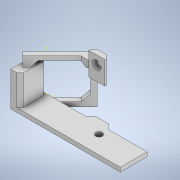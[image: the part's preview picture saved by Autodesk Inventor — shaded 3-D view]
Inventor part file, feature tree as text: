
AUTODESK INVENTOR PART (.ipt)
format: ipt  version: 2021.2 (Build 252289000, 289)  size: 273,408 bytes
history: native  units: in
note: dims shown in document units (in); Inventor stores cm internally (conversion verified against a paired STEP export)
features: sketch x20, extrude x15, chamfer x4
ambient origin geometry x8: Origin, YZ Plane, XZ Plane, XY Plane, X Axis, Y Axis, Z Axis, Center Point
bodies: Solid1 (feature_tree)
feature tree (39):
  extrude  "Extrusion1"  Depth=0.16in
  extrude  "Extrusion2"  Depth=1.0in
  chamfer  "Chamfer1"  Distance=0.1875in
  extrude  "Extrusion3"  Depth=0.125in TaperAngle=0.0deg
  extrude  "Extrusion4"  Depth=0.125in TaperAngle=0.0deg
  sketch  "Sketch5"  dims[d9=0.125in d10=0.125in d11=45.0deg d12=0.5625in d13=0.0in]
  chamfer  "Chamfer2"  Distance=0.125in Angle=45.0deg
  sketch  "Sketch6"  dims[d14=0.33in d15=0.5625in d16=0.0in d17=0.125in d18=0.125in d19=45.0deg]
  extrude  "Extrusion5"  Depth=0.816in
  sketch  "Sketch8"  dims[d23=0.1in d24=0.0in d26=0.2875in d27=0.0in]
  extrude  "Extrusion6"  Depth=0.1in TaperAngle=0.0deg
  extrude  "Extrusion7"  Depth=1.7875in TaperAngle=0.0deg
  sketch  "Sketch11"  dims[d36=21112.9in d37=0.0in d38=1.5in d39=0.0in]
  extrude  "Extrusion8"  Depth=0.35in TaperAngle=0.0deg
  extrude  "Extrusion9"  Depth=1.5in TaperAngle=0.0deg
  extrude  "Extrusion10"  Depth=1.01in TaperAngle=0.0deg
  extrude  "Extrusion11"  Depth=0.1875in TaperAngle=45.0deg
  sketch  "Sketch16"
  extrude  "Extrusion12"  Depth=1.0in TaperAngle=0.0deg
  extrude  "Extrusion13"  [1 undecoded]
  extrude  "Extrusion14"  [1 undecoded]
  chamfer  "Chamfer3"  [1 undecoded]
  chamfer  "Chamfer4"  [1 undecoded]
  extrude  "Extrusion15"  [1 undecoded]
  sketch  "Sketch1"  dims[d0=3.75in d1=0.16in]
  sketch  "Sketch2"  dims[d2=1.0in d3=0.0in d4=0.3in]
  sketch  "Sketch3"  dims[d5=0.3in]
  sketch  "Sketch4"  dims[d6=1.8in d7=0.1875in d8=0.0in]
  sketch  "Sketch7"  dims[d20=0.5625in d21=0.0in d22=0.816in]
  sketch  "Sketch9"  dims[d28=0.9125in d29=0.0in d30=1.7875in d31=0.0in]
  sketch  "Sketch10"  dims[d32=0.225in d33=0.0in d34=0.35in d35=0.0in]
  sketch  "Sketch12"  dims[d41=0.16in d42=1.01in d43=0.0in]
  sketch  "Sketch13"  dims[d44=0.25in d45=0.125in d46=45.0deg d47=0.1875in d48=0.125in d49=45.0deg]
  sketch  "Sketch14"  dims[d53=0.25in d54=1.0in d55=0.0in]
  sketch  "Sketch15"
  sketch  "Sketch17"
  sketch  "Sketch18"
  sketch  "Sketch19"
  sketch  "Sketch20"
note: 5 required parameter values undecoded (feature->parameter linkage not recoverable at this tier; creation-order binding heuristic only, values carry confidence <= 0.55)
